# Revit family: Unterlegscheibe
name_source: partatom
category: HLS-Bauteile
revit_build: Autodesk Revit 2017 (Build: 20190507_1515(x64)
units: mm (PartAtom-declared; Revit-internal decimal feet)

## family parameters
Arbeitsebenenbasiert = Ja
Beim Laden mit Abzugskörper schneiden = Nein
Bemaßung runder Anschluss = Durchmesser verwenden
Gemeinsam genutzt = Ja
Immer vertikal = Nein
Raumberechnungspunkt = Nein
Teiletyp = Normal

## types (17) — shared parameters
Fabrikat = MEFA
Firma = MEFA Befestigungs- und Montagesysteme GmbH
Material = Stahl
Mengeneinheit = St
Oberflaeche = galvanisch verzinkt
Vorgabe-Ansicht = 1219 mm
vpe = 100 St

## per-type parameters (varying)
| type | Abmessung | Artikelnummer | Ausführung | Außendurchmesser | D | D0 | EAN | Gewicht | Gewicht pro Bauteil | Innendurchmesser | Kurztext1 | Kurztext2 | Länge | Stärke |
| Unterlegscheibe  6,4x12x1,6 | 6,4 x 12,0 x 1,6 mm | 4320247 |  | 12 mm  [stored 0.0393701 ft] | 12 mm  [stored 0.0393701 ft] | 6 mm  [stored 0.019685 ft] | 4250928439024 | 0.00 kg | 0.00 kg | 6 mm  [stored 0.019685 ft] | Unterlegscheibe EN ISO 7089 | 6,4 x 12,0 x 1,6 mm gvz | 2 mm  [stored 0.00656168 ft] | 2 mm  [stored 0.00656168 ft] |
| Unterlegscheibe  8,4x16x1,6 | 8,4 x 16 x 1,6 mm | 4320255 |  | 16 mm  [stored 0.0524934 ft] | 16 mm  [stored 0.0524934 ft] | 8 mm  [stored 0.0262467 ft] | 4250928439031 | 0.00 kg | 0.00 kg | 8 mm  [stored 0.0262467 ft] | Unterlegscheibe EN ISO 7089 | 8,4 x 16 x 1,6 mm gvz | 2 mm  [stored 0.00656168 ft] | 2 mm  [stored 0.00656168 ft] |
| Unterlegscheibe 10,5x20x2,0 | 10,5 x 20 x 2 mm | 4320263 |  | 20 mm  [stored 0.0656168 ft] | 20 mm  [stored 0.0656168 ft] | 11 mm | 4250928439048 | 0.00 kg | 0.00 kg | 11 mm | Unterlegscheibe EN ISO 7089 | 10,5 x 20 x 2 mm gvz | 2 mm  [stored 0.00656168 ft] | 2 mm  [stored 0.00656168 ft] |
| Unterlegscheibe 13,0x24x2,5 | 13 x 24 x 2,5 mm | 4320271 |  | 24 mm  [stored 0.0787402 ft] | 24 mm  [stored 0.0787402 ft] | 13 mm | 4250928439055 | 0.01 kg | 0.01 kg | 13 mm | Unterlegscheibe EN ISO 7089 | 13 x 24 x 2,5 mm gvz | 3 mm  [stored 0.00984252 ft] | 3 mm  [stored 0.00984252 ft] |
| Unterlegscheibe, verstärkt  5,3x15x1,2 | 5,3 x 15 x 1,6 mm | 4330226 | verstärkt | 15 mm  [stored 0.0492126 ft] | 15 mm  [stored 0.0492126 ft] | 5 mm  [stored 0.0164042 ft] | 4250928439062 | 0.00 kg | 0.00 kg | 5 mm  [stored 0.0164042 ft] | Unterlegscheibe EN ISO 7093-1 | 5,3 x 15 x 1,6 mm gvz | 1 mm  [stored 0.00328084 ft] | 2 mm  [stored 0.00656168 ft] |
| Unterlegscheibe, verstärkt  6,4x18x1,6 | 6,4 x 18 x 1,6 mm | 4330242 | verstärkt | 18 mm  [stored 0.0590551 ft] | 18 mm  [stored 0.0590551 ft] | 6 mm  [stored 0.019685 ft] | 4250928439079 | 0.00 kg | 0.00 kg | 6 mm  [stored 0.019685 ft] | Unterlegscheibe EN ISO 7093-1 | 6,4 x 18 x 1,6 mm gvz | 2 mm  [stored 0.00656168 ft] | 2 mm  [stored 0.00656168 ft] |
| Unterlegscheibe, verstärkt  8,4x24x2,0 | 8,4 x 24 x 2 mm | 4330250 | verstärkt | 24 mm  [stored 0.0787402 ft] | 24 mm  [stored 0.0787402 ft] | 8 mm  [stored 0.0262467 ft] | 4250928439086 | 0.01 kg | 0.01 kg | 8 mm  [stored 0.0262467 ft] | Unterlegscheibe EN ISO 7093-1 | 8,4 x 24 x 2 mm gvz | 2 mm  [stored 0.00656168 ft] | 2 mm  [stored 0.00656168 ft] |
| Unterlegscheibe, verstärkt 10,5x30x2,5 | 10,5 x 30 x 2,5 mm | 4330269 | verstärkt | 30 mm  [stored 0.0984252 ft] | 30 mm  [stored 0.0984252 ft] | 11 mm | 4250928439093 | 0.01 kg | 0.01 kg | 11 mm | Unterlegscheibe EN ISO 7093-1 | 10,5 x 30 x 2,5 mm gvz | 3 mm  [stored 0.00984252 ft] | 3 mm  [stored 0.00984252 ft] |
| Unterlegscheibe, verstärkt 13,0x37x3,0 | 13 x 37 x 3 mm | 4330277 | verstärkt | 37 mm  [stored 0.121391 ft] | 37 mm  [stored 0.121391 ft] | 13 mm | 4250928439109 | 0.02 kg | 0.02 kg | 13 mm | Unterlegscheibe EN ISO 7093-1 | 13 x 37 x 3 mm gvz | 3 mm  [stored 0.00984252 ft] | 3 mm  [stored 0.00984252 ft] |
| Unterlegscheibe, verstärkt 17,0x50x3,0 | 17 x 50 x 3 mm | 4330285 | verstärkt | 50 mm  [stored 0.164042 ft] | 50 mm  [stored 0.164042 ft] | 17 mm | 4250928439116 | 0.04 kg | 0.04 kg | 17 mm | Unterlegscheibe EN ISO 7093-1 | 17 x 50 x 3 mm gvz | 3 mm  [stored 0.00984252 ft] | 3 mm  [stored 0.00984252 ft] |
| Unterlegscheibe, verstärkt  8,4x35x3,0 | 8,4 x 35 x 3 mm | 4350847 | verstärkt | 35 mm  [stored 0.114829 ft] | 35 mm  [stored 0.114829 ft] | 8 mm  [stored 0.0262467 ft] | 4250928439260 | 0.02 kg | 0.02 kg | 8 mm  [stored 0.0262467 ft] | Unterlegscheibe verstärkt | 8,4 x 35 x 3 mm gvz | 3 mm  [stored 0.00984252 ft] | 3 mm  [stored 0.00984252 ft] |
| Unterlegscheibe, verstärkt 10,5x35x3,0 | 10,5 x 35 x 3 mm | 4351053 | verstärkt | 35 mm  [stored 0.114829 ft] | 35 mm  [stored 0.114829 ft] | 11 mm | 4250928439284 | 0.02 kg | 0.02 kg | 11 mm | Unterlegscheibe verstärkt | 10,5 x 35 x 3 mm gvz | 3 mm  [stored 0.00984252 ft] | 3 mm  [stored 0.00984252 ft] |
| Unterlegscheibe, verstärkt 13,0x30x2,5 | 13 x 30 x 2,5 mm | 4351282 | verstärkt | 30 mm  [stored 0.0984252 ft] | 30 mm  [stored 0.0984252 ft] | 13 mm | 4250928439307 | 0.01 kg | 0.01 kg | 13 mm | Unterlegscheibe verstärkt | 13 x 30 x 2,5 mm gvz | 3 mm  [stored 0.00984252 ft] | 3 mm  [stored 0.00984252 ft] |
| Unterlegscheibe, verstärkt  8,4x44x3,5 | 8,4 x 44 x 3,5 mm | 4350850 | verstärkt | 44 mm  [stored 0.144357 ft] | 44 mm  [stored 0.144357 ft] | 8 mm  [stored 0.0262467 ft] | 4250928439277 | 0.04 kg | 0.04 kg | 8 mm  [stored 0.0262467 ft] | Unterlegscheibe verstärkt | 8,4 x 44 x 3,5 mm gvz | 4 mm  [stored 0.0131234 ft] | 4 mm  [stored 0.0131234 ft] |
| Unterlegscheibe, verstärkt 10,5x44x3,5 | 10,5 x 44 x 3,5 mm | 4351059 | verstärkt | 44 mm  [stored 0.144357 ft] | 44 mm  [stored 0.144357 ft] | 11 mm | 4250928439291 | 0.04 kg | 0.04 kg | 11 mm | Unterlegscheibe verstärkt | 10,5 x 44 x 3,5 mm gvz | 4 mm  [stored 0.0131234 ft] | 4 mm  [stored 0.0131234 ft] |
| Unterlegscheibe, verstärkt 13,5x44x3,5 | 13,5 x 44 x 3,5 mm | 4351344 | verstärkt | 44 mm  [stored 0.144357 ft] | 44 mm  [stored 0.144357 ft] | 14 mm  [stored 0.0459318 ft] | 4250928439314 | 0.04 kg | 0.04 kg | 14 mm  [stored 0.0459318 ft] | Unterlegscheibe verstärkt | 13,5 x 44 x 3,5 mm gvz | 4 mm  [stored 0.0131234 ft] | 4 mm  [stored 0.0131234 ft] |
| Unterlegscheibe, verstärkt 17,0x44x3,5 | 17 x 44 x 3,5 mm | 4351744 | verstärkt | 44 mm  [stored 0.144357 ft] | 44 mm  [stored 0.144357 ft] | 17 mm | 4250928439321 | 0.04 kg | 0.04 kg | 17 mm | Unterlegscheibe verstärkt | 17 x 44 x 3,5 mm gvz | 4 mm  [stored 0.0131234 ft] | 4 mm  [stored 0.0131234 ft] |

note: [stored X ft] marks values corroborated as IEEE doubles in the binary element streams (Revit-internal decimal feet)
